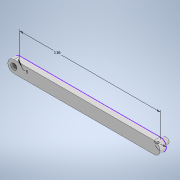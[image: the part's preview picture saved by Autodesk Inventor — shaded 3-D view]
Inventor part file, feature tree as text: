
AUTODESK INVENTOR PART (.ipt)
format: ipt  version: 2022 (Build 260153000, 153)  size: 105,472 bytes
history: native  units: mm
features: extrude x2, sketch x1
ambient origin geometry x8: Origin, YZ Plane, XZ Plane, XY Plane, X Axis, Y Axis, Z Axis, Center Point
bodies: Solid1 (feature_tree)
feature tree (3):
  sketch  "Sketch1"  dims[d0=10.0mm d1=5.0mm d2=116.0mm d3=5.0mm d4=0.0mm d5=5.0mm d6=0.0mm]
  extrude  "Extrusion1"  Depth=5.0mm
  extrude  "Extrusion2"  Depth=5.0mm
